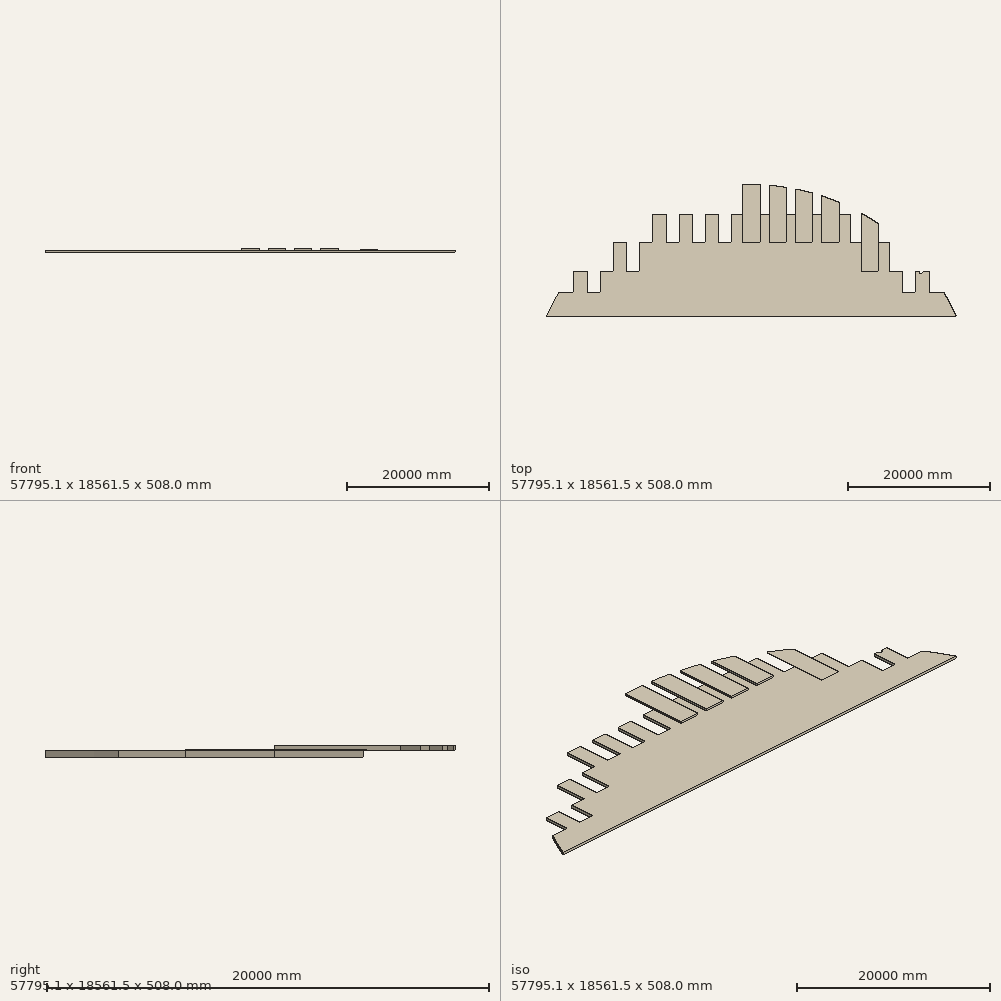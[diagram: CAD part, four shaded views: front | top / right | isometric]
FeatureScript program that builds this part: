
annotation { "Feature Type Name" : "Feature", "Feature Type Description" : "" }
export const myFeature = defineFeature(function(context is Context, id is Id, definition is map)
    precondition{}
    {
        {
            var Q0;
            Q0=qCreatedBy(makeId("Top.planeOp"),FACE);
            var sketch = newSketch(context, id + "F0", { "sketchPlane" : qUnion([Q0])});
            skLineSegment(sketch, "E0", {"start": v(-13905.13, 27592.02) * mm, "end": v(-12050.93, 27592.02) * mm});
            skLineSegment(sketch, "E1", {"start": v(-13905.13, 27592.02) * mm, "end": v(-13905.13, 28571.37) * mm});
            skLineSegment(sketch, "E2.1.0.0", {"start": v(-12050.93, 27592.02) * mm, "end": v(-12050.93, 29401.55) * mm});
            skLineSegment(sketch, "E2.2.0.0", {"start": v(-10196.73, 27592.02) * mm, "end": v(-10196.73, 30094.9) * mm});
            skLineSegment(sketch, "E2.3.0.0", {"start": v(-8342.53, 27592.02) * mm, "end": v(-8342.53, 30660.7) * mm});
            skLineSegment(sketch, "E2.4.0.0", {"start": v(-6488.33, 27592.02) * mm, "end": v(-6488.33, 31105.9) * mm});
            skLineSegment(sketch, "E2.5.0.0", {"start": v(-4634.13, 27592.02) * mm, "end": v(-4634.13, 31435.66) * mm});
            skLineSegment(sketch, "E2.6.0.0", {"start": v(-2779.93, 27592.02) * mm, "end": v(-2779.93, 31653.56) * mm});
            skLineSegment(sketch, "E2.7.0.0", {"start": v(-925.73, 27592.02) * mm, "end": v(-925.73, 31761.91) * mm});
            skLineSegment(sketch, "E2.8.0.0", {"start": v(928.47, 27592.02) * mm, "end": v(928.47, 31761.83) * mm});
            skLineSegment(sketch, "E2.9.0.0", {"start": v(2782.67, 27592.02) * mm, "end": v(2782.67, 31653.32) * mm});
            skLineSegment(sketch, "E2.10.0.0", {"start": v(4636.87, 27592.02) * mm, "end": v(4636.87, 31435.26) * mm});
            skLineSegment(sketch, "E2.11.0.0", {"start": v(6491.07, 27592.02) * mm, "end": v(6491.07, 31105.34) * mm});
            skLineSegment(sketch, "E2.12.0.0", {"start": v(8345.27, 27592.02) * mm, "end": v(8345.27, 30659.95) * mm});
            skLineSegment(sketch, "E2.13.0.0", {"start": v(10199.47, 27592.02) * mm, "end": v(10199.47, 30093.97) * mm});
            skLineSegment(sketch, "E2.14.0.0", {"start": v(12053.67, 27592.02) * mm, "end": v(12053.67, 29400.43) * mm});
            skLineSegment(sketch, "E2.15.0.0", {"start": v(13907.87, 27592.02) * mm, "end": v(13907.87, 28570.04) * mm});
            skLineSegment(sketch, "E2.direction1", {"start": v(-13905.13, 27592.02) * mm, "end": v(-12050.93, 27592.02) * mm, "construction": true});
            skPoint(sketch, "E3.orphan", {"position": v(13907.87, 36428.98) * mm});
            skPoint(sketch, "E4.orphan", {"position": v(12053.67, 36428.98) * mm});
            skPoint(sketch, "E5.orphan", {"position": v(10199.47, 36428.98) * mm});
            skPoint(sketch, "E6.orphan", {"position": v(8345.27, 36428.98) * mm});
            skPoint(sketch, "E7.orphan", {"position": v(6491.07, 36428.98) * mm});
            skPoint(sketch, "E8.orphan", {"position": v(4636.87, 36428.98) * mm});
            skPoint(sketch, "E9.orphan", {"position": v(2782.67, 36428.98) * mm});
            skPoint(sketch, "E10.orphan", {"position": v(928.47, 36428.98) * mm});
            skPoint(sketch, "E11.orphan", {"position": v(-925.73, 36428.98) * mm});
            skPoint(sketch, "E12.orphan", {"position": v(-2779.93, 36428.98) * mm});
            skPoint(sketch, "E13.orphan", {"position": v(-4634.13, 36428.98) * mm});
            skPoint(sketch, "E14.orphan", {"position": v(-6488.33, 36428.98) * mm});
            skPoint(sketch, "E15.orphan", {"position": v(-8342.53, 36428.98) * mm});
            skPoint(sketch, "E16.orphan", {"position": v(-10196.73, 36428.98) * mm});
            skPoint(sketch, "E17.orphan", {"position": v(-12050.93, 36428.98) * mm});
            skPoint(sketch, "E18.orphan", {"position": v(-13905.13, 36428.98) * mm});
            skCircle(sketch, "E19", {"center": v(0, 30997.94) * mm, "radius": 304.8 * mm});
            skLineSegment(sketch, "E20", {"start": v(-19469.1, 23558.3) * mm, "end": v(-17613.53, 23558.3) * mm});
            skLineSegment(sketch, "E21", {"start": v(-15759.33, 27592.02) * mm, "end": v(-15759.33, 23558.3) * mm});
            skLineSegment(sketch, "E22.1.0.0", {"start": v(-13905.13, 27592.02) * mm, "end": v(-13905.13, 23558.3) * mm});
            skLineSegment(sketch, "E22.2.0.0", {"start": v(-12050.93, 27592.02) * mm, "end": v(-12050.93, 23558.3) * mm});
            skLineSegment(sketch, "E22.3.0.0", {"start": v(-10196.73, 27592.02) * mm, "end": v(-10196.73, 23558.3) * mm});
            skLineSegment(sketch, "E22.4.0.0", {"start": v(-8342.53, 27592.02) * mm, "end": v(-8342.53, 23558.3) * mm});
            skLineSegment(sketch, "E22.5.0.0", {"start": v(-6488.33, 27592.02) * mm, "end": v(-6488.33, 23558.3) * mm});
            skLineSegment(sketch, "E22.6.0.0", {"start": v(-4634.13, 27592.02) * mm, "end": v(-4634.13, 23558.3) * mm});
            skLineSegment(sketch, "E22.7.0.0", {"start": v(-2779.93, 27592.02) * mm, "end": v(-2779.93, 23558.3) * mm});
            skLineSegment(sketch, "E22.8.0.0", {"start": v(-925.73, 27592.02) * mm, "end": v(-925.73, 23558.3) * mm});
            skLineSegment(sketch, "E22.9.0.0", {"start": v(928.47, 27592.02) * mm, "end": v(928.47, 23558.3) * mm});
            skLineSegment(sketch, "E22.10.0.0", {"start": v(2782.67, 27592.02) * mm, "end": v(2782.67, 23558.3) * mm});
            skLineSegment(sketch, "E22.11.0.0", {"start": v(4636.87, 27592.02) * mm, "end": v(4636.87, 23558.3) * mm});
            skLineSegment(sketch, "E22.12.0.0", {"start": v(6491.07, 27592.02) * mm, "end": v(6491.07, 23558.3) * mm});
            skLineSegment(sketch, "E22.13.0.0", {"start": v(8345.27, 27592.02) * mm, "end": v(8345.27, 23558.3) * mm});
            skLineSegment(sketch, "E22.14.0.0", {"start": v(10199.47, 27592.02) * mm, "end": v(10199.47, 23558.3) * mm});
            skLineSegment(sketch, "E22.15.0.0", {"start": v(12053.67, 27592.02) * mm, "end": v(12053.67, 23558.3) * mm});
            skLineSegment(sketch, "E22.16.0.0", {"start": v(13907.87, 27592.02) * mm, "end": v(13907.87, 23558.3) * mm});
            skLineSegment(sketch, "E22.17.0.0", {"start": v(15762.07, 27592.02) * mm, "end": v(15762.07, 23558.3) * mm});
            skLineSegment(sketch, "E22.18.0.0", {"start": v(17616.27, 26445.1) * mm, "end": v(17616.27, 23558.3) * mm});
            skLineSegment(sketch, "E22.direction1", {"start": v(-15759.33, 23558.3) * mm, "end": v(-13905.13, 23558.3) * mm, "construction": true});
            skLineSegment(sketch, "E23", {"start": v(-17613.53, 23558.3) * mm, "end": v(-17613.53, 26446.92) * mm});
            skLineSegment(sketch, "E24", {"start": v(-19467.73, 23558.3) * mm, "end": v(-19467.73, 25113.41) * mm});
            skLineSegment(sketch, "E25.trimOffspring", {"start": v(928.47, 27592.02) * mm, "end": v(2782.67, 27592.02) * mm});
            skLineSegment(sketch, "E26.trimOffspring", {"start": v(4636.87, 27592.02) * mm, "end": v(6491.07, 27592.02) * mm});
            skLineSegment(sketch, "E27.trimOffspring", {"start": v(8345.27, 27592.02) * mm, "end": v(10199.47, 27592.02) * mm});
            skLineSegment(sketch, "E28", {"start": v(19470.47, 23558.3) * mm, "end": v(19470.47, 25111.29) * mm});
            skPoint(sketch, "E29.orphan", {"position": v(17616.27, 27592.02) * mm});
            skLineSegment(sketch, "E30.trimOffspring", {"start": v(12053.67, 27592.02) * mm, "end": v(13907.87, 27592.02) * mm});
            skLineSegment(sketch, "E31.trimOffspring", {"start": v(-2779.93, 27592.02) * mm, "end": v(-925.73, 27592.02) * mm});
            skLineSegment(sketch, "E32.trimOffspring", {"start": v(-6488.33, 27592.02) * mm, "end": v(-4634.13, 27592.02) * mm});
            skLineSegment(sketch, "E33.trimOffspring", {"start": v(-10196.73, 27592.02) * mm, "end": v(-8342.53, 27592.02) * mm});
            skLineSegment(sketch, "E34", {"start": v(-925.73, 24237.75) * mm, "end": v(928.47, 24237.75) * mm});
            skLineSegment(sketch, "E35", {"start": v(-25031.7, 19572.69) * mm, "end": v(-23177.5, 19572.69) * mm});
            skLineSegment(sketch, "E36", {"start": v(-21323.3, 23558.3) * mm, "end": v(-21323.3, 19572.69) * mm});
            skLineSegment(sketch, "E37.1.0.0", {"start": v(-19469.1, 23558.3) * mm, "end": v(-19469.1, 19572.69) * mm});
            skLineSegment(sketch, "E37.2.0.0", {"start": v(-17614.9, 23558.3) * mm, "end": v(-17614.9, 19572.69) * mm});
            skLineSegment(sketch, "E37.3.0.0", {"start": v(-15760.7, 23558.3) * mm, "end": v(-15760.7, 19572.69) * mm});
            skLineSegment(sketch, "E37.4.0.0", {"start": v(-13906.5, 23558.3) * mm, "end": v(-13906.5, 19572.69) * mm});
            skLineSegment(sketch, "E37.5.0.0", {"start": v(-12052.3, 23558.3) * mm, "end": v(-12052.3, 19572.69) * mm});
            skLineSegment(sketch, "E37.6.0.0", {"start": v(-10198.1, 23558.3) * mm, "end": v(-10198.1, 19572.69) * mm});
            skLineSegment(sketch, "E37.7.0.0", {"start": v(-8343.9, 23558.3) * mm, "end": v(-8343.9, 19572.69) * mm});
            skLineSegment(sketch, "E37.8.0.0", {"start": v(-6489.7, 23558.3) * mm, "end": v(-6489.7, 19572.69) * mm});
            skLineSegment(sketch, "E37.9.0.0", {"start": v(-4635.5, 23558.3) * mm, "end": v(-4635.5, 19572.69) * mm});
            skLineSegment(sketch, "E37.10.0.0", {"start": v(-2781.3, 23558.3) * mm, "end": v(-2781.3, 19572.69) * mm});
            skLineSegment(sketch, "E37.11.0.0", {"start": v(-927.1, 23558.3) * mm, "end": v(-927.1, 19572.69) * mm});
            skLineSegment(sketch, "E37.12.0.0", {"start": v(927.1, 23558.3) * mm, "end": v(927.1, 19572.69) * mm});
            skLineSegment(sketch, "E37.13.0.0", {"start": v(2781.3, 23558.3) * mm, "end": v(2781.3, 19572.69) * mm});
            skLineSegment(sketch, "E37.14.0.0", {"start": v(4635.5, 23558.3) * mm, "end": v(4635.5, 19572.69) * mm});
            skLineSegment(sketch, "E37.15.0.0", {"start": v(6489.7, 23558.3) * mm, "end": v(6489.7, 19572.69) * mm});
            skLineSegment(sketch, "E37.16.0.0", {"start": v(8343.9, 23558.3) * mm, "end": v(8343.9, 19572.69) * mm});
            skLineSegment(sketch, "E37.17.0.0", {"start": v(10198.1, 23558.3) * mm, "end": v(10198.1, 19572.69) * mm});
            skLineSegment(sketch, "E37.18.0.0", {"start": v(12052.3, 23558.3) * mm, "end": v(12052.3, 19572.69) * mm});
            skLineSegment(sketch, "E37.19.0.0", {"start": v(13906.5, 23558.3) * mm, "end": v(13906.5, 19572.69) * mm});
            skLineSegment(sketch, "E37.20.0.0", {"start": v(15760.7, 23558.3) * mm, "end": v(15760.7, 19572.69) * mm});
            skLineSegment(sketch, "E37.21.0.0", {"start": v(17614.9, 23558.3) * mm, "end": v(17614.9, 19572.69) * mm});
            skLineSegment(sketch, "E37.direction1", {"start": v(-21323.3, 19572.69) * mm, "end": v(-19469.1, 19572.69) * mm, "construction": true});
            skLineSegment(sketch, "E38.0.22.0", {"start": v(19469.1, 23558.3) * mm, "end": v(19469.1, 19572.69) * mm});
            skLineSegment(sketch, "E38.0.23.0", {"start": v(21323.3, 23558.3) * mm, "end": v(21323.3, 19572.69) * mm});
            skLineSegment(sketch, "E38.0.24.0", {"start": v(23177.5, 21736.58) * mm, "end": v(23177.5, 19572.69) * mm});
            skLineSegment(sketch, "E39", {"start": v(-23177.5, 19572.69) * mm, "end": v(-23177.5, 21736.6) * mm});
            skCircle(sketch, "E40", {"center": v(23923.77, 19572.69) * mm, "radius": 304.8 * mm});
            skLineSegment(sketch, "E41.trimOffspring", {"start": v(21323.3, 23558.3) * mm, "end": v(21323.3, 23558.3) * mm});
            skLineSegment(sketch, "E42.trimOffspring", {"start": v(17614.9, 23558.3) * mm, "end": v(19470.47, 23558.3) * mm});
            skLineSegment(sketch, "E43.trimOffspring", {"start": v(-15760.7, 23558.3) * mm, "end": v(-13905.13, 23558.3) * mm});
            skLineSegment(sketch, "E44.trimOffspring", {"start": v(-12052.3, 23558.3) * mm, "end": v(-10198.1, 23558.3) * mm});
            skLineSegment(sketch, "E45.trimOffspring", {"start": v(-8343.9, 23558.3) * mm, "end": v(-6488.33, 23558.3) * mm});
            skLineSegment(sketch, "E46.trimOffspring", {"start": v(-927.1, 23558.3) * mm, "end": v(928.47, 23558.3) * mm});
            skLineSegment(sketch, "E47.trimOffspring", {"start": v(2781.3, 23558.3) * mm, "end": v(4636.87, 23558.3) * mm});
            skLineSegment(sketch, "E48.trimOffspring", {"start": v(6489.7, 23558.3) * mm, "end": v(8345.27, 23558.3) * mm});
            skLineSegment(sketch, "E49.trimOffspring", {"start": v(10198.1, 23558.3) * mm, "end": v(12053.67, 23558.3) * mm});
            skLineSegment(sketch, "E50.trimOffspring", {"start": v(13906.5, 23558.3) * mm, "end": v(15762.07, 23558.3) * mm});
            skLineSegment(sketch, "E51.trimOffspring", {"start": v(19469.1, 19572.69) * mm, "end": v(21323.3, 19572.69) * mm});
            skLineSegment(sketch, "E52.trimOffspring", {"start": v(-17614.9, 19572.69) * mm, "end": v(-15760.7, 19572.69) * mm});
            skLineSegment(sketch, "E53.trimOffspring", {"start": v(-13906.5, 19572.69) * mm, "end": v(-12052.3, 19572.69) * mm});
            skLineSegment(sketch, "E54.trimOffspring", {"start": v(-10198.1, 19572.69) * mm, "end": v(-8343.9, 19572.69) * mm});
            skLineSegment(sketch, "E55.trimOffspring", {"start": v(-4635.5, 23558.3) * mm, "end": v(-2779.93, 23558.3) * mm});
            skLineSegment(sketch, "E56.trimOffspring", {"start": v(-6489.7, 19572.69) * mm, "end": v(-4635.5, 19572.69) * mm});
            skLineSegment(sketch, "E57.trimOffspring", {"start": v(-2781.3, 19572.69) * mm, "end": v(-927.1, 19572.69) * mm});
            skLineSegment(sketch, "E58.trimOffspring", {"start": v(927.1, 19572.69) * mm, "end": v(2781.3, 19572.69) * mm});
            skLineSegment(sketch, "E59.trimOffspring", {"start": v(4635.5, 19572.69) * mm, "end": v(6489.7, 19572.69) * mm});
            skLineSegment(sketch, "E60.trimOffspring", {"start": v(8343.9, 19572.69) * mm, "end": v(10198.1, 19572.69) * mm});
            skLineSegment(sketch, "E61.trimOffspring", {"start": v(12052.3, 19572.69) * mm, "end": v(13906.5, 19572.69) * mm});
            skLineSegment(sketch, "E62.trimOffspring", {"start": v(15760.7, 19572.69) * mm, "end": v(17614.9, 19572.69) * mm});
            skLineSegment(sketch, "E63.trimOffspring", {"start": v(23177.5, 19572.69) * mm, "end": v(25031.7, 19572.69) * mm});
            skLineSegment(sketch, "E64.trimOffspring", {"start": v(-21323.3, 19572.69) * mm, "end": v(-19469.1, 19572.69) * mm});
            skArc(sketch, "E65", {"start": v(25031.7, 19572.69) * mm, "mid": v(13506.25, 28762.08) * mm, "end": v(-925.73, 31761.91) * mm});
            skArc(sketch, "E66", {"start": v(-8342.53, 30660.7) * mm, "mid": v(-17583.96, 26466.59) * mm, "end": v(-25031.7, 19572.69) * mm});
            skArc(sketch, "E67", {"start": v(-2779.93, 31653.56) * mm, "mid": v(-15161.09, 27925.21) * mm, "end": v(-25031.7, 19572.69) * mm});
            skArc(sketch, "E68", {"start": v(928.47, 31761.83) * mm, "mid": v(-927.31, 31761.87) * mm, "end": v(-2779.93, 31653.56) * mm});
            skArc(sketch, "E69", {"start": v(-25031.7, 19572.69) * mm, "mid": v(-27151.4, 16506.88) * mm, "end": v(-28897.53, 13213.96) * mm});
            skArc(sketch, "E70", {"start": v(21323.3, 23558.3) * mm, "mid": v(25637.57, 18772.1) * mm, "end": v(28897.55, 13213.96) * mm});
            skLineSegment(sketch, "E71", {"start": v(-28897.53, 13213.96) * mm, "end": v(28897.55, 13213.96) * mm});
            skLineSegment(sketch, "E72", {"start": v(-23177.5, 16506.88) * mm, "end": v(-21323.3, 16506.88) * mm});
            skLineSegment(sketch, "E73", {"start": v(-23177.5, 19572.69) * mm, "end": v(-23177.5, 16506.88) * mm});
            skLineSegment(sketch, "E74", {"start": v(-21323.3, 19572.69) * mm, "end": v(-21323.3, 16506.88) * mm});
            skLineSegment(sketch, "E75", {"start": v(21323.3, 19572.69) * mm, "end": v(21323.3, 16506.88) * mm});
            skLineSegment(sketch, "E76", {"start": v(23177.5, 19572.69) * mm, "end": v(23177.5, 16506.88) * mm});
            skLineSegment(sketch, "E77", {"start": v(-25031.7, 19572.69) * mm, "end": v(-25031.7, 16506.88) * mm});
            skLineSegment(sketch, "E78", {"start": v(25031.7, 19572.69) * mm, "end": v(25031.7, 16506.88) * mm});
            skPoint(sketch, "E79.orphan", {"position": v(-27151.4, 16506.88) * mm});
            skLineSegment(sketch, "E80.trimOffspring", {"start": v(21323.3, 16506.88) * mm, "end": v(27151.42, 16506.88) * mm});
            skLineSegment(sketch, "E81", {"start": v(-10196.73, 23558.3) * mm, "end": v(-12050.93, 23558.3) * mm});
            skLineSegment(sketch, "E82", {"start": v(-27151.4, 16506.88) * mm, "end": v(-21323.3, 16506.88) * mm});
            skSolve(sketch);
        }
        {
            var Q0;
            {var subQ21=sQuery(id+"F0.wireOp",EDGE,"E37.1.0.0");Q0=makeQuery(id+"F0.imprint","IMPRINT",FACE,{"disambiguationData":[TD([[makeQuery(id+"F0.imprint","IMPRINT",EDGE,{"derivedFrom":subQ21}),1.0]])]});}
            var Q1;
            Q1=makeQuery(id+"F0.imprint","IMPRINT",FACE,{"disambiguationData":[TD([[makeQuery(id+"F0.imprint","IMPRINT",EDGE,{"derivedFrom":sQuery(id+"F0.wireOp",EDGE,"E35")}),-1.0]])]});
            var Q2;
            Q2=makeQuery(id+"F0.imprint","IMPRINT",FACE,{"disambiguationData":[TD([[makeQuery(id+"F0.imprint","IMPRINT",EDGE,{"derivedFrom":sQuery(id+"F0.wireOp",EDGE,"E0")}),-1.0]])]});
            var Q3;
            Q3=makeQuery(id+"F0.imprint","IMPRINT",FACE,{"disambiguationData":[TD([[makeQuery(id+"F0.imprint","IMPRINT",EDGE,{"derivedFrom":sQuery(id+"F0.wireOp",EDGE,"E33.trimOffspring")}),-1.0]])]});
            var Q4;
            {var subQ1=sQuery(id+"F0.wireOp",EDGE,"E22.5.0.0");Q4=makeQuery(id+"F0.imprint","IMPRINT",FACE,{"disambiguationData":[TD([[makeQuery(id+"F0.imprint","IMPRINT",EDGE,{"derivedFrom":subQ1}),1.0]])]});}
            var Q5;
            {var subQ5=sQuery(id+"F0.wireOp",EDGE,"E22.7.0.0");Q5=makeQuery(id+"F0.imprint","IMPRINT",FACE,{"disambiguationData":[TD([[makeQuery(id+"F0.imprint","IMPRINT",EDGE,{"derivedFrom":subQ5}),1.0]])]});}
            var Q6;
            {var subQ0=sQuery(id+"F0.wireOp",EDGE,"E22.10.0.0");Q6=makeQuery(id+"F0.imprint","IMPRINT",FACE,{"disambiguationData":[TD([[makeQuery(id+"F0.imprint","IMPRINT",EDGE,{"derivedFrom":subQ0}),-1.0]])]});}
            var Q7;
            {var subQ2=sQuery(id+"F0.wireOp",EDGE,"E22.11.0.0");Q7=makeQuery(id+"F0.imprint","IMPRINT",FACE,{"disambiguationData":[TD([[makeQuery(id+"F0.imprint","IMPRINT",EDGE,{"derivedFrom":subQ2}),1.0]])]});}
            var Q8;
            {var subQ3=sQuery(id+"F0.wireOp",EDGE,"E22.13.0.0");Q8=makeQuery(id+"F0.imprint","IMPRINT",FACE,{"disambiguationData":[TD([[makeQuery(id+"F0.imprint","IMPRINT",EDGE,{"derivedFrom":subQ3}),1.0]])]});}
            var Q9;
            {var subQ2=sQuery(id+"F0.wireOp",EDGE,"E22.15.0.0");Q9=makeQuery(id+"F0.imprint","IMPRINT",FACE,{"disambiguationData":[TD([[makeQuery(id+"F0.imprint","IMPRINT",EDGE,{"derivedFrom":subQ2}),1.0]])]});}
            var Q10;
            {var subQ0=sQuery(id+"F0.wireOp",EDGE,"E76");Q10=makeQuery(id+"F0.imprint","IMPRINT",FACE,{"disambiguationData":[TD([[makeQuery(id+"F0.imprint","IMPRINT",EDGE,{"derivedFrom":subQ0}),1.0]])]});}
            extrude(context, id + "F1", {"entities" : qUnion([Q0, Q1, Q2, Q3, Q4, Q5, Q6, Q7, Q8, Q9, Q10]), "depth" : 304.8 * mm});
        }
        {
            var Q0;
            Q0=makeQuery(id+"F1.opExtrude","CAP_FACE",FACE,{"disambiguationData":[OSD([sQuery(id+"F0.wireOp",EDGE,"E0"),sQuery(id+"F0.wireOp",EDGE,"E20"),sQuery(id+"F0.wireOp",EDGE,"E22.1.0.0"),sQuery(id+"F0.wireOp",EDGE,"E22.2.0.0"),sQuery(id+"F0.wireOp",EDGE,"E22.5.0.0"),sQuery(id+"F0.wireOp",EDGE,"E22.6.0.0"),sQuery(id+"F0.wireOp",EDGE,"E22.7.0.0"),sQuery(id+"F0.wireOp",EDGE,"E22.8.0.0"),sQuery(id+"F0.wireOp",EDGE,"E22.9.0.0"),sQuery(id+"F0.wireOp",EDGE,"E22.10.0.0"),sQuery(id+"F0.wireOp",EDGE,"E22.11.0.0"),sQuery(id+"F0.wireOp",EDGE,"E22.12.0.0"),sQuery(id+"F0.wireOp",EDGE,"E22.13.0.0"),sQuery(id+"F0.wireOp",EDGE,"E22.14.0.0"),sQuery(id+"F0.wireOp",EDGE,"E22.15.0.0"),sQuery(id+"F0.wireOp",EDGE,"E22.16.0.0"),sQuery(id+"F0.wireOp",EDGE,"E25.trimOffspring"),sQuery(id+"F0.wireOp",EDGE,"E26.trimOffspring"),sQuery(id+"F0.wireOp",EDGE,"E27.trimOffspring"),sQuery(id+"F0.wireOp",EDGE,"E30.trimOffspring"),sQuery(id+"F0.wireOp",EDGE,"E31.trimOffspring"),sQuery(id+"F0.wireOp",EDGE,"E32.trimOffspring"),sQuery(id+"F0.wireOp",EDGE,"E33.trimOffspring"),sQuery(id+"F0.wireOp",EDGE,"E35"),sQuery(id+"F0.wireOp",EDGE,"E37.1.0.0"),sQuery(id+"F0.wireOp",EDGE,"E37.2.0.0"),sQuery(id+"F0.wireOp",EDGE,"E37.3.0.0"),sQuery(id+"F0.wireOp",EDGE,"E37.20.0.0"),sQuery(id+"F0.wireOp",EDGE,"E37.21.0.0"),sQuery(id+"F0.wireOp",EDGE,"E38.0.22.0"),sQuery(id+"F0.wireOp",EDGE,"E40"),sQuery(id+"F0.wireOp",EDGE,"E42.trimOffspring"),sQuery(id+"F0.wireOp",EDGE,"E43.trimOffspring"),sQuery(id+"F0.wireOp",EDGE,"E45.trimOffspring"),sQuery(id+"F0.wireOp",EDGE,"E46.trimOffspring"),sQuery(id+"F0.wireOp",EDGE,"E47.trimOffspring"),sQuery(id+"F0.wireOp",EDGE,"E48.trimOffspring"),sQuery(id+"F0.wireOp",EDGE,"E49.trimOffspring"),sQuery(id+"F0.wireOp",EDGE,"E50.trimOffspring"),sQuery(id+"F0.wireOp",EDGE,"E51.trimOffspring"),sQuery(id+"F0.wireOp",EDGE,"E52.trimOffspring"),sQuery(id+"F0.wireOp",EDGE,"E55.trimOffspring"),sQuery(id+"F0.wireOp",EDGE,"E62.trimOffspring"),sQuery(id+"F0.wireOp",EDGE,"E63.trimOffspring"),sQuery(id+"F0.wireOp",EDGE,"E64.trimOffspring"),sQuery(id+"F0.wireOp",EDGE,"E69"),sQuery(id+"F0.wireOp",EDGE,"E70"),sQuery(id+"F0.wireOp",EDGE,"E71"),sQuery(id+"F0.wireOp",EDGE,"E73"),sQuery(id+"F0.wireOp",EDGE,"E74"),sQuery(id+"F0.wireOp",EDGE,"E75"),sQuery(id+"F0.wireOp",EDGE,"E76"),sQuery(id+"F0.wireOp",EDGE,"E77"),sQuery(id+"F0.wireOp",EDGE,"E78"),sQuery(id+"F0.wireOp",EDGE,"E80.trimOffspring"),sQuery(id+"F0.wireOp",EDGE,"E22.4.0.0"),sQuery(id+"F0.wireOp",EDGE,"E22.3.0.0"),sQuery(id+"F0.wireOp",EDGE,"E81"),sQuery(id+"F0.wireOp",EDGE,"E82")])],"isStart":false});
            var sketch = newSketch(context, id + "F2", { "sketchPlane" : qUnion([Q0])});
            skArc(sketch, "E83", {"start": v(28897.55, 13213.96) * mm, "mid": v(0, 31775.42) * mm, "end": v(-28897.53, 13213.96) * mm});
            skLineSegment(sketch, "E84", {"start": v(0, 23558.3) * mm, "end": v(1219.2, 23558.3) * mm});
            skLineSegment(sketch, "E85", {"start": v(0, 23558.3) * mm, "end": v(-1219.2, 23558.3) * mm});
            skLineSegment(sketch, "E86", {"start": v(1219.2, 23558.3) * mm, "end": v(1219.2, 31752.02) * mm});
            skLineSegment(sketch, "E87", {"start": v(-1219.2, 23558.3) * mm, "end": v(-1219.2, 31752.02) * mm});
            skLineSegment(sketch, "E88", {"start": v(3709.77, 23558.3) * mm, "end": v(2490.57, 23558.3) * mm});
            skLineSegment(sketch, "E89", {"start": v(3709.77, 23558.3) * mm, "end": v(4928.97, 23558.3) * mm});
            skLineSegment(sketch, "E90", {"start": v(2490.57, 23558.3) * mm, "end": v(2490.57, 31677.66) * mm});
            skLineSegment(sketch, "E91", {"start": v(4928.97, 23558.3) * mm, "end": v(4928.97, 31390.8) * mm});
            skLineSegment(sketch, "E92", {"start": v(7418.17, 23558.3) * mm, "end": v(6198.97, 23558.3) * mm});
            skLineSegment(sketch, "E93", {"start": v(7418.17, 23558.3) * mm, "end": v(8637.37, 23558.3) * mm});
            skLineSegment(sketch, "E94", {"start": v(6198.97, 23558.3) * mm, "end": v(6198.97, 31164.88) * mm});
            skLineSegment(sketch, "E95", {"start": v(8637.37, 23558.3) * mm, "end": v(8637.37, 30578.96) * mm});
            skLineSegment(sketch, "E96", {"start": v(11126.57, 23558.3) * mm, "end": v(9907.37, 23558.3) * mm});
            skLineSegment(sketch, "E97", {"start": v(11126.57, 23558.3) * mm, "end": v(12345.77, 23558.3) * mm});
            skLineSegment(sketch, "E98", {"start": v(9907.37, 23558.3) * mm, "end": v(9907.37, 30191.4) * mm});
            skLineSegment(sketch, "E99", {"start": v(12345.77, 23558.3) * mm, "end": v(12345.77, 29278.99) * mm});
            skLineSegment(sketch, "E100", {"start": v(16687.8, 19572.69) * mm, "end": v(15468.6, 19572.69) * mm});
            skPoint(sketch, "E100.endSnap0", {"position": v(16687.8, 19572.69) * mm});
            skLineSegment(sketch, "E101", {"start": v(16687.8, 19572.69) * mm, "end": v(17907, 19572.69) * mm});
            skLineSegment(sketch, "E102", {"start": v(17907, 19572.69) * mm, "end": v(17907, 26249.12) * mm});
            skLineSegment(sketch, "E103", {"start": v(15468.6, 19572.69) * mm, "end": v(15468.6, 27756.07) * mm});
            skSolve(sketch);
        }
        {
            var Q0;
            {var subQ1=makeQuery(id+"F1.opExtrude","CAP_EDGE",EDGE,{"disambiguationData":[OSD([sQuery(id+"F0.wireOp",EDGE,"E22.8.0.0")])],"isStart":false});Q0=makeQuery(id+"F2.imprint","IMPRINT",FACE,{"disambiguationData":[TD([[makeQuery(id+"F2.imprint","IMPRINT",EDGE,{"derivedFrom":subQ1}),1.0]])]});}
            var Q1;
            {var subQ1=makeQuery(id+"F1.opExtrude","CAP_EDGE",EDGE,{"disambiguationData":[OSD([sQuery(id+"F0.wireOp",EDGE,"E22.8.0.0")])],"isStart":false});Q1=makeQuery(id+"F2.imprint","IMPRINT",FACE,{"disambiguationData":[TD([[makeQuery(id+"F2.imprint","IMPRINT",EDGE,{"derivedFrom":subQ1}),-1.0]])]});}
            var Q2;
            {var subQ1=makeQuery(id+"F1.opExtrude","CAP_EDGE",EDGE,{"disambiguationData":[OSD([sQuery(id+"F0.wireOp",EDGE,"E22.9.0.0")])],"isStart":false});Q2=makeQuery(id+"F2.imprint","IMPRINT",FACE,{"disambiguationData":[TD([[makeQuery(id+"F2.imprint","IMPRINT",EDGE,{"derivedFrom":subQ1}),1.0]])]});}
            extrude(context, id + "F3", {"entities" : qUnion([Q0, Q1, Q2]), "depth" : 203.2 * mm});
        }
        {
            var Q0;
            {var subQ4=makeQuery(id+"F1.opExtrude","CAP_EDGE",EDGE,{"disambiguationData":[OSD([sQuery(id+"F0.wireOp",EDGE,"E22.10.0.0")])],"isStart":false});Q0=makeQuery(id+"F2.imprint","IMPRINT",FACE,{"disambiguationData":[TD([[makeQuery(id+"F2.imprint","IMPRINT",EDGE,{"derivedFrom":subQ4}),1.0]])]});}
            var Q1;
            {var subQ1=makeQuery(id+"F1.opExtrude","CAP_EDGE",EDGE,{"disambiguationData":[OSD([sQuery(id+"F0.wireOp",EDGE,"E22.10.0.0")])],"isStart":false});Q1=makeQuery(id+"F2.imprint","IMPRINT",FACE,{"disambiguationData":[TD([[makeQuery(id+"F2.imprint","IMPRINT",EDGE,{"derivedFrom":subQ1}),-1.0]])]});}
            var Q2;
            {var subQ1=makeQuery(id+"F1.opExtrude","CAP_EDGE",EDGE,{"disambiguationData":[OSD([sQuery(id+"F0.wireOp",EDGE,"E22.11.0.0")])],"isStart":false});Q2=makeQuery(id+"F2.imprint","IMPRINT",FACE,{"disambiguationData":[TD([[makeQuery(id+"F2.imprint","IMPRINT",EDGE,{"derivedFrom":subQ1}),1.0]])]});}
            extrude(context, id + "F4", {"entities" : qUnion([Q0, Q1, Q2]), "depth" : 203.2 * mm});
        }
        {
            var Q0;
            {var subQ9=makeQuery(id+"F1.opExtrude","CAP_EDGE",EDGE,{"disambiguationData":[OSD([sQuery(id+"F0.wireOp",EDGE,"E22.12.0.0")])],"isStart":false});Q0=makeQuery(id+"F2.imprint","IMPRINT",FACE,{"disambiguationData":[TD([[makeQuery(id+"F2.imprint","IMPRINT",EDGE,{"derivedFrom":subQ9}),1.0]])]});}
            var Q1;
            {var subQ1=makeQuery(id+"F1.opExtrude","CAP_EDGE",EDGE,{"disambiguationData":[OSD([sQuery(id+"F0.wireOp",EDGE,"E22.12.0.0")])],"isStart":false});Q1=makeQuery(id+"F2.imprint","IMPRINT",FACE,{"disambiguationData":[TD([[makeQuery(id+"F2.imprint","IMPRINT",EDGE,{"derivedFrom":subQ1}),-1.0]])]});}
            var Q2;
            {var subQ1=makeQuery(id+"F1.opExtrude","CAP_EDGE",EDGE,{"disambiguationData":[OSD([sQuery(id+"F0.wireOp",EDGE,"E22.13.0.0")])],"isStart":false});Q2=makeQuery(id+"F2.imprint","IMPRINT",FACE,{"disambiguationData":[TD([[makeQuery(id+"F2.imprint","IMPRINT",EDGE,{"derivedFrom":subQ1}),1.0]])]});}
            extrude(context, id + "F5", {"entities" : qUnion([Q0, Q1, Q2]), "depth" : 203.2 * mm});
        }
        {
            var Q0;
            {var subQ4=makeQuery(id+"F1.opExtrude","CAP_EDGE",EDGE,{"disambiguationData":[OSD([sQuery(id+"F0.wireOp",EDGE,"E22.14.0.0")])],"isStart":false});Q0=makeQuery(id+"F2.imprint","IMPRINT",FACE,{"disambiguationData":[TD([[makeQuery(id+"F2.imprint","IMPRINT",EDGE,{"derivedFrom":subQ4}),1.0]])]});}
            var Q1;
            {var subQ1=makeQuery(id+"F1.opExtrude","CAP_EDGE",EDGE,{"disambiguationData":[OSD([sQuery(id+"F0.wireOp",EDGE,"E22.14.0.0")])],"isStart":false});Q1=makeQuery(id+"F2.imprint","IMPRINT",FACE,{"disambiguationData":[TD([[makeQuery(id+"F2.imprint","IMPRINT",EDGE,{"derivedFrom":subQ1}),-1.0]])]});}
            var Q2;
            {var subQ1=makeQuery(id+"F1.opExtrude","CAP_EDGE",EDGE,{"disambiguationData":[OSD([sQuery(id+"F0.wireOp",EDGE,"E22.15.0.0")])],"isStart":false});Q2=makeQuery(id+"F2.imprint","IMPRINT",FACE,{"disambiguationData":[TD([[makeQuery(id+"F2.imprint","IMPRINT",EDGE,{"derivedFrom":subQ1}),1.0]])]});}
            extrude(context, id + "F6", {"entities" : qUnion([Q0, Q1, Q2]), "depth" : 203.2 * mm});
        }
        {
            var Q0;
            {var subQ5=makeQuery(id+"F1.opExtrude","CAP_EDGE",EDGE,{"disambiguationData":[OSD([sQuery(id+"F0.wireOp",EDGE,"E37.20.0.0")])],"isStart":false});Q0=makeQuery(id+"F2.imprint","IMPRINT",FACE,{"disambiguationData":[TD([[makeQuery(id+"F2.imprint","IMPRINT",EDGE,{"derivedFrom":subQ5}),1.0]])]});}
            var Q1;
            {var subQ1=makeQuery(id+"F1.opExtrude","CAP_EDGE",EDGE,{"disambiguationData":[OSD([sQuery(id+"F0.wireOp",EDGE,"E37.20.0.0")])],"isStart":false});Q1=makeQuery(id+"F2.imprint","IMPRINT",FACE,{"disambiguationData":[TD([[makeQuery(id+"F2.imprint","IMPRINT",EDGE,{"derivedFrom":subQ1}),-1.0]])]});}
            var Q2;
            {var subQ1=makeQuery(id+"F1.opExtrude","CAP_EDGE",EDGE,{"disambiguationData":[OSD([sQuery(id+"F0.wireOp",EDGE,"E37.21.0.0")])],"isStart":false});Q2=makeQuery(id+"F2.imprint","IMPRINT",FACE,{"disambiguationData":[TD([[makeQuery(id+"F2.imprint","IMPRINT",EDGE,{"derivedFrom":subQ1}),1.0]])]});}
            extrude(context, id + "F7", {"entities" : qUnion([Q0, Q1, Q2]), "depth" : 25.4 * mm});
        }
    });
